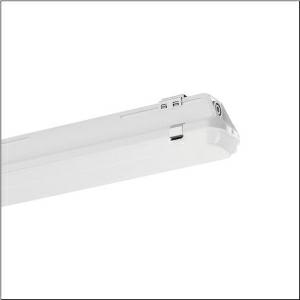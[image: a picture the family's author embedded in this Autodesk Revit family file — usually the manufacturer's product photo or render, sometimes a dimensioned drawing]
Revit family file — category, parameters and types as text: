
# Revit family: monsun_r__12_51fp107p4b0q_7abb
name_source: partatom
category: Lighting Fixtures
units: mm (PartAtom-declared; Revit-internal decimal feet)

## family parameters
Cut with Voids When Loaded = No
Host = Face
Light Source = No
Part Type = Normal
Room Calculation Point = No
Round Connector Dimension = Use Diameter
Shared = No

## types (1)
- Monsun® 12 (1 x LED, 12070 lm, 66.2 W, 4000K)
    Apparent Load = 66 VA
    CIE Flux Codes = 47 76 93 94 100
    Color Rendering = 80
    Color Temperature = 4000K
    Default Elevation = 1800 mm
    Description = Monsun® 12, damp-proof luminaire, chain hanger, primary optical cover: enclosure, of PMMA, light emission: direct distribution, primary light characteristic: symmetric, installation type: suspended mounting, surface-mounted, horizontal mounting, vertical mounting, LED rated luminous flux: 12.070 lm, light colour: 840, colour temperature: 4000K, control gear: ECG, with terminal, 3-pole, max. 2.5mm², mains connection: 220..240V, AC, 50/60Hz, rated input power: 66W, luminaire housing, of glass-fibre reinforced polyester, uncoated, bright grey, length: 1.590 mm, width: 90 mm, height: 88mm, clip for enclosure, of stainless steel (V2A), ceiling mounting element, of stainless steel (V2A), chain hanger, of stainless steel (V2A), protection rating (complete): IP66, insulation class (complete): insulation class I (protective earthing), certification: CE, ENEC, VDE, protection symbol: D, impact resistance: IK04, permissible ambient temperature for indoor applications: -35..+35°C, standard: EN 50419, EN 60598-2-1, no direct snow, no direct sun, no direct rain, for indoor or canopied outdoor use, corresponds to IFS (International Featured Standards) requirements for safety and quality in the food industry, for animal farming (ammonia tested): for use in cowhouse, pig house, horse-stables... (not for use in poultry stables), AT max for animal farming = 40°C, packaging unit: 1 piece
    Height = 89 mm
    Lamp = 1 x LED
    Lamp Light Flux = 12070 lm
    Lamp Power = 66.2 W
    Lamp count = 1
    Length = 1590 mm
    Luminous efficacy = 182 lm/W
    Manufacturer = Siteco
    ModVariant = No
    Model = 51FP107P4B0Q
    Mounting Place = Ceiling
    Mounting Type = Pendant
    Number of Poles = 1
    OnlyDefault = Yes
    Power Factor = 1
    Product Name = Monsun® 12
    Product group = damp-proof luminaire | ceiling pendant
    ProductGroupID = 908
    Protection Class = Protection class I
    Protection Degree = IP 66
    RLX_Detail_Level = 1
    RlxData = <blob elided: 88461 chars, md5=d82cfb09>
    Socket = socket
    Standby Power = 0 W
    System Light Flux = 12070 lm
    System Power = 66 W
    Type Comments = Product without accessories
    Type Image = l_1004748.jpg
    URL = http://relux.com
    VarID = ---
    Voltage = 0 V
    Weight = 0.00 kg
    Width = 90 mm

## geometry (parser evidence)
native form markers: Blend x4, Sweep x15
no freeform markers — native parametric forms only
